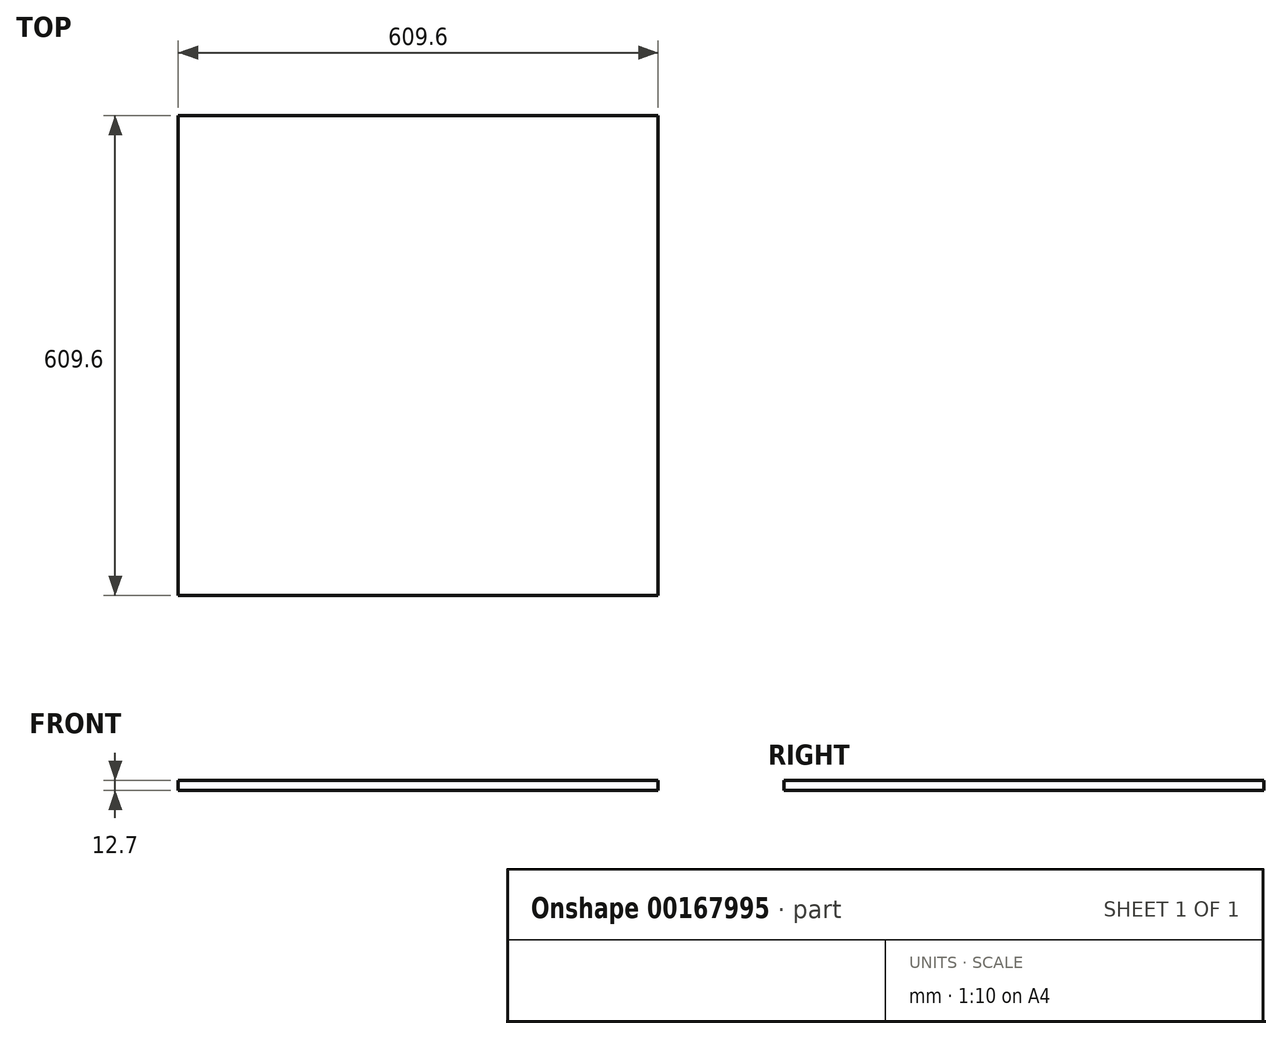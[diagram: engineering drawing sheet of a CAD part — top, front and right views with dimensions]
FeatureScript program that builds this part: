
annotation { "Feature Type Name" : "Feature", "Feature Type Description" : "" }
export const myFeature = defineFeature(function(context is Context, id is Id, definition is map)
    precondition{}
    {
        {
            var Q0;
            Q0=qCreatedBy(makeId("Top.planeOp"),FACE);
            var sketch = newSketch(context, id + "F0", { "sketchPlane" : qUnion([Q0])});
            skLineSegment(sketch, "E0.bottom", {"start": v(-43.54, 558.8) * mm, "end": v(566.06, 558.8) * mm});
            skLineSegment(sketch, "E0.top", {"start": v(-43.54, -50.8) * mm, "end": v(566.06, -50.8) * mm});
            skLineSegment(sketch, "E0.left", {"start": v(-43.54, 558.8) * mm, "end": v(-43.54, -50.8) * mm});
            skLineSegment(sketch, "E0.right", {"start": v(566.06, 558.8) * mm, "end": v(566.06, -50.8) * mm});
            skSolve(sketch);
        }
        {
            var Q0;
            Q0=makeQuery(id+"F0.imprint","IMPRINT",FACE,{"disambiguationData":[TD([[makeQuery(id+"F0.imprint","IMPRINT",EDGE,{"derivedFrom":sQuery(id+"F0.wireOp",EDGE,"E0.bottom")}),-1.0]])]});
            extrude(context, id + "F1", {"entities" : qUnion([Q0]), "depth" : 12.7 * mm});
        }
    });
